# Revit family: 44350230(2021)
name_source: partatom
category: Plumbing Fixtures
revit_build: Autodesk Revit 2018 (Build: 20170223_1515(x64)
units: mm (PartAtom-declared; Revit-internal decimal feet)

## family parameters
Always vertical = Yes
Cut with Voids When Loaded = No
OmniClass Number = 23.45.55.00
OmniClass Title = Sanitary Faucets, Wastes
Part Type = Normal
Room Calculation Point = No
Round Connector Dimension = Use Diameter
Shared = No
Work Plane-Based = No

## types (1)
- 44350230 Shower system
    2D/3D/BIM Files URL = http://static.hansa.com
    3D View = https://static.hansa.com
    Advanced Features = Flexible length / can be shortened
    Ambience photo = http://static.hansa.com
    Approval ABP = P-IX 29855/IAS
    AssetType = Fixed
    BIMObjectName = 44350230(2021)
    Backflow Prevention EN1717 = EB
    BodyMaterial = Brass
    Brand = HANSA
    Catalog Drawing URL = http://static.hansa.com
    Category = Shower
    CloseOffRating = 0
    Color = Chrome
    Connection = Eccentric coupling(s);External thread;Cover plate(s);Silencer(s)
    Connection Size = G1/2
    Dimension Drawing URL = http://static.hansa.com
    Diverter = Turn operated diverter;Integrated into flow control handle
    DurationUnit = Year
    EAN Number = 4057304015960
    EN Standard = EN 1112, EN 1113, EN 1111
    ETIM Class Number = EC011329 Shower mixing tap
    FDV Document URL = http://www.hansa.com
    FaucetMainMaterial = Brass
    Features = Thermostatic
    Finish = Polished
    Flow Drawing URL = http://static.hansa.com
    Flow Rate At 300kPa = 30.3 L/s
    FlowCoefficient = 0
    Group = Shower system
    Hand Shower Size = Ø 95 mm
    IfcExportAs = IfcValveType
    IfcExportType = FAUCET
    Installation Type = Wall mounted
    Installation Width = CC150± 3 mm
    Installation and Maintenance Guide URL = http://static.hansa.com
    Interactive AR View URL = https://static.hansa.com
    Lever Handle = Temperature control handle;Flow control handle
    Manufacturer = HANSA
    ManufacturerName = HANSA
    ManufacturerURL = http://www.hansa.com
    Market = International;Germany;Austria;Switzerland;Belgium;Netherlands;France;Czech Republic;Slovakia;Hungary;Romania;Italy;Spain;Greece;Portugal;Australia
    Material = Brass
    Max. Hot Water Supply = 65 °C
    Mechanical Parts = Ceramic head part for flow control;Thermostatic cartridge for automatic temperature control;Non-return valve(s);Litter filter(s)
    Mobile Product Information URL = http://mpi.hansa.com
    Model = 44350230 Shower system
    ModelReference = 44350230
    NBSDescription = Shower mixers
    NBSReference = 45-35-70/335
    Name = 44350230 Shower system
    Name_en = 44350230 Shower system
    Noise Class = I (ISO 3822)
    NominalDepth = 546 mm
    NominalHeight = 1165 mm
    NominalWidth = 291 mm
    Over Head Shower Size = 200x200 mm
    Pressure Loss With Flow 02ls = 180000.0 Pa
    Product Code = 44350230
    Product Family = HANSAMICRA Style
    Product Image URL = http://static.hansa.com
    Product URL = http://static.hansa.com
    Revision = 1
    Sales Package dimensions (LxWxH) = 1154 x 383 x 98
    Shape = Sculptured
    Shower Parts = Hand shower;Shower rail;Overhead shower;Adjustable shower rail bracket;Shower hose (1750 mm);Eco flow control;Variable fixing points;Rotatable ball joint connection;Anti limescale technology (easy to clean)
    Shower Spray = Normal;Refreshing;Relaxing
    Shower Spray Number = 3 shower sprays
    ShowerDefaultElevation = 900 mm
    Size = 290x545x1165 mm
    Spare-Part Information URL = http://static.hansa.com
    Spout Projection = 445 - 470 mm
    Surface treatment = Chrome
    Technical DataSheet URL = http://www.hansa.com
    Temperature Adjustments = Safety stop against scalding at 38°C;The housing of the fittings conducts minimal heat
    UNSPSC Class Number = 30181805 Combination fixed and hand held shower head
    URL ABP = http://static.hansa.com
    URL Declaration of Conformity = http://static.hansa.com
    URL REACH = http://static.hansa.com
    Uniclass2 = Pr_40_30_96_81
    Uniclass2015Description = Shower thermostatic water supply sets
    Uniclass2015Reference = Pr_40_20_87_81
    Version = 2
    VersionDate = 01/07/2022
    Warranty Information URL = http://warranty.hansa.com
    WarrantyDescription = http://warranty.hansa.com
    WarrantyDurationUnit = Year
    Working Pressure = 100 - 1000 kPa
    WorkingPressure = 100 - 1000 kPa

## geometry (parser evidence)
native form markers: Sweep x6
no freeform markers — native parametric forms only
